# Revit family: Boiler_Eutectic-Cast-Iron_GT 330A _DDR-Americas_2016
name_source: partatom
category: Equipement de génie climatique
revit_build: Autodesk Revit 2016 (Build: 20161004_0715(x64)
units: mm (PartAtom-declared; Revit-internal decimal feet)

## family parameters
Basée sur le plan de construction = Non
Cote de connecteur circulaire = Utiliser le diamètre
Couper avec des vides une fois chargée = Non
Numéro OmniClass = 23.75.10.11.14.11
Partagée = Non
Point de calcul de pièce = Non
Titre OmniClass = Cast-Iron Boilers
Toujours verticalement = Oui
Type d'élément = Normal

## types (6) — shared parameters
04 CSI = 23 52 23
95 CSI = 15510
ASME Rating MAWP = 90
Approvals = CSA, MASS, NY-DEP, ASME, CSD-1, Low Nox certified, CRN
Category = Mechanical Equipment
Code d'assemblage = D3020100
Description = Near-Condensing Eutectic Cast Iron Boiler
Efficiency = 88.00%
Fabricant = De Dietrich Boilers / DDR Americas Inc.
Firing Turndown Ratio = 5:1
Frequency = 60 Hz
Full Load Amps = <12A
Gas Pressure = 7-14 Inches w.c.
Gas-vent Category = I, II, III, IV, Sidewall vented and Direct vent (sealed combustion air)
Heat Exchanger Material = Cast Iron
Installation/Operating Instructions = http://www.dedietrichboilers.com
Low Nox - Optional = Oui
Manufacturer Fax = 519-650-1709
Max Water Temp Safety Limit = 248 °F
Nominal Height = 51 "
Nominal Width = 31.5 "
Phase = 1
Piping Layout = http://www.dedietrichboilers.com
Product Brochure = http://www.dedietrichboilers.com
Product Page URL = http://www.dedietrichboilers.com
SMARTBIM Object Version = 3
SMARTBIM URL = http://www.SMARTBIM.com
Specifications URL = http://www.dedietrichboilers.com
Subcategory = Gas-Oil Fired Eutectic Cast Iron Boiler
URL = http://www.dedietrichboilers.com
Voltage = 120 V
Water Operating Temp Range °F /°C = 104-212°F / 40-100°C
zero-valued in all types: Gas Connection

## per-type parameters (varying)
| type | # Sections | #2 Fuel Oil Input | Boiler-vent Connection | Dry Weight | Gas Input | Installed Weight | Nominal Length | Output [Gas-Oil] | Radius | Unit | Water Capacity | Water Resistance Delta T -18 F (Ft. H2O) | Water Resistance Delta T -27 F (Ft. H2O) | Water Resistance Delta T -36 F (Ft. H2O) |
| GT 334A | 4 | 2.8 USG | 7 " | 1349.00 lb | 118 kW | 1555 | 39 " | 100.8 kW | 3.5 " | Paint Ivory Glossy | 25.4 gal | 0.483 | 0.215 | 0.121 |
| GT 335A | 5 | 4.15 USG | 7 " | 1623.00 lb | 175 kW | 1880 | 45.3 " | 149.4 kW | 3.5 " | Aluminum Polished | 30.7 gal | 1.026 | 0.457 | 0.256 |
| GT 336A | 6 | 5.6 USG | 7 " | 1865.00 lb | 237 kW | 2165 | 51.6 " | 201.6 kW | 3.5 " | Aluminum Polished | 36.0 gal | 2.099 | 0.933 | 0.525 |
| GT 337A | 7 | 7.1 USG | 8 " | 2163.00 lb | 300 kW | 2505 | 57.9 " | 255.7 kW | 4 " | Aluminum Polished | 41.2 gal | 3.055 | 1.358 | 0.764 |
| GT 338A | 8 | 8.5 USG | 8 " | 2432.00 lb | 359 kW | 2825 | 64.2 " | 306.1 kW | 4 " | Aluminum Polished | 46.5 gal | 4.38 | 1.945 | 1.094 |
| GT 339A | 9 | 10 USG | 8 " | 2712.00 lb | 423 kW | 3145 | 70.5 " | 360.1 kW | 4 " | Aluminum Polished | 51.8 gal | 6.332 | 2.818 | 1.583 |

note: column(s) folded — value = type name in every type: Modèle

## geometry (parser evidence)
native form markers: Blend x24, Sweep x4
no freeform markers — native parametric forms only
